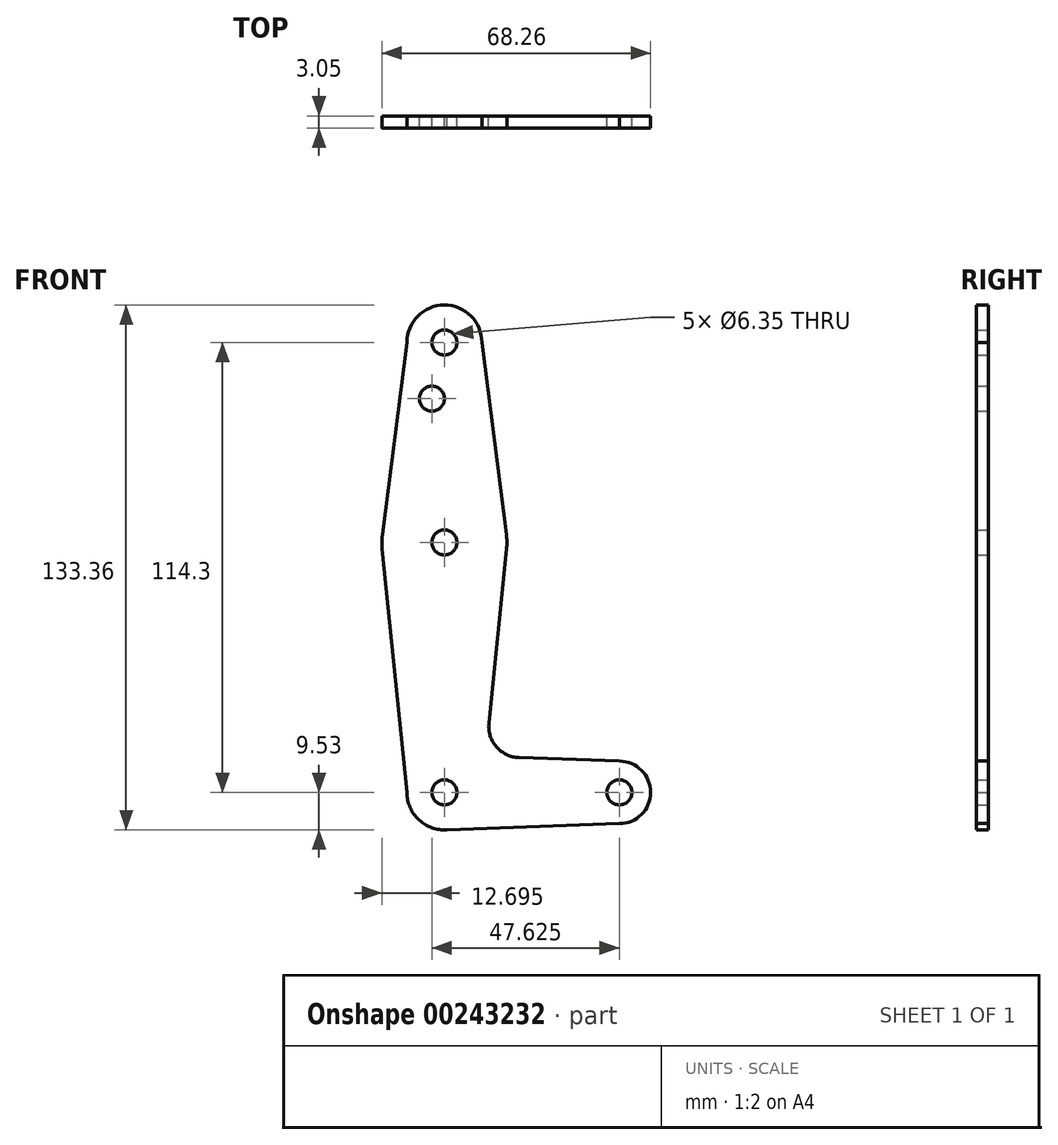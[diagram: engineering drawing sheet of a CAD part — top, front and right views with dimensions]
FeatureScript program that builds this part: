
annotation { "Feature Type Name" : "Feature", "Feature Type Description" : "" }
export const myFeature = defineFeature(function(context is Context, id is Id, definition is map)
    precondition{}
    {
        {
            var Q0;
            Q0=qCreatedBy(makeId("Front.planeOp"),FACE);
            var sketch = newSketch(context, id + "F0", { "sketchPlane" : qUnion([Q0])});
            skCircle(sketch, "E0", {"center": v(0, 114.3) * mm, "radius": 9.52 * mm});
            skCircle(sketch, "E1", {"center": v(0, 63.5) * mm, "radius": 15.88 * mm});
            skCircle(sketch, "E2", {"center": v(0, 0) * mm, "radius": 9.53 * mm});
            skCircle(sketch, "E3", {"center": v(44.45, 0) * mm, "radius": 7.94 * mm});
            skLineSegment(sketch, "E4", {"start": v(0, 114.3) * mm, "end": v(0, 63.5) * mm});
            skLineSegment(sketch, "E5", {"start": v(0, 63.5) * mm, "end": v(0, 0) * mm});
            skLineSegment(sketch, "E6", {"start": v(0, 0) * mm, "end": v(44.45, 0) * mm});
            skCircle(sketch, "E7", {"center": v(0, 114.3) * mm, "radius": 3.18 * mm});
            skCircle(sketch, "E8", {"center": v(0, 63.5) * mm, "radius": 3.18 * mm});
            skCircle(sketch, "E9", {"center": v(0, 0) * mm, "radius": 3.18 * mm});
            skCircle(sketch, "E10", {"center": v(44.45, 0) * mm, "radius": 3.18 * mm});
            skLineSegment(sketch, "E11", {"start": v(-9.53, 114.3) * mm, "end": v(-15.75, 65.5) * mm});
            skLineSegment(sketch, "E12", {"start": v(11.3, 17.6) * mm, "end": v(15.8, 61.9) * mm});
            skLineSegment(sketch, "E13", {"start": v(9.52, 114.3) * mm, "end": v(15.75, 65.5) * mm});
            skLineSegment(sketch, "E14", {"start": v(18.93, 8.85) * mm, "end": v(44.45, 7.94) * mm});
            skLineSegment(sketch, "E15", {"start": v(0, -9.53) * mm, "end": v(44.45, -7.94) * mm});
            skPoint(sketch, "E16.newPointA", {"position": v(9.52, 0) * mm});
            skArc(sketch, "E16.filletArc", {"start": v(11.3, 17.6) * mm, "mid": v(13.22, 11.57) * mm, "end": v(18.93, 8.85) * mm});
            skCircle(sketch, "E17", {"center": v(-3.17, 100.03) * mm, "radius": 3.18 * mm});
            skLineSegment(sketch, "E18", {"start": v(-15.8, 61.9) * mm, "end": v(-9.53, 0) * mm});
            skSolve(sketch);
        }
        {
            var Q0;
            Q0 = qSketchRegion(id + "F0", true);
            var Q1;
            {var subQ0=sQuery(id+"F0.wireOp",EDGE,"E5");var subQ1=sQuery(id+"F0.wireOp",EDGE,"E2");var subQ2=makeQuery(id+"F0.imprint","INTERSECT",VERTEX,{"derivedFrom":[subQ1,subQ0]});Q1=makeQuery(id+"F0.imprint","IMPRINT",FACE,{"disambiguationData":[TD([[makeQuery(id+"F0.imprint","IMPRINT",EDGE,{"disambiguationData":[TD([[subQ2,1.0]])],"derivedFrom":subQ1}),1.0]])]});}
            extrude(context, id + "F1", {"entities" : qUnion([Q0, Q1]), "depth" : 3.05 * mm});
        }
    });
